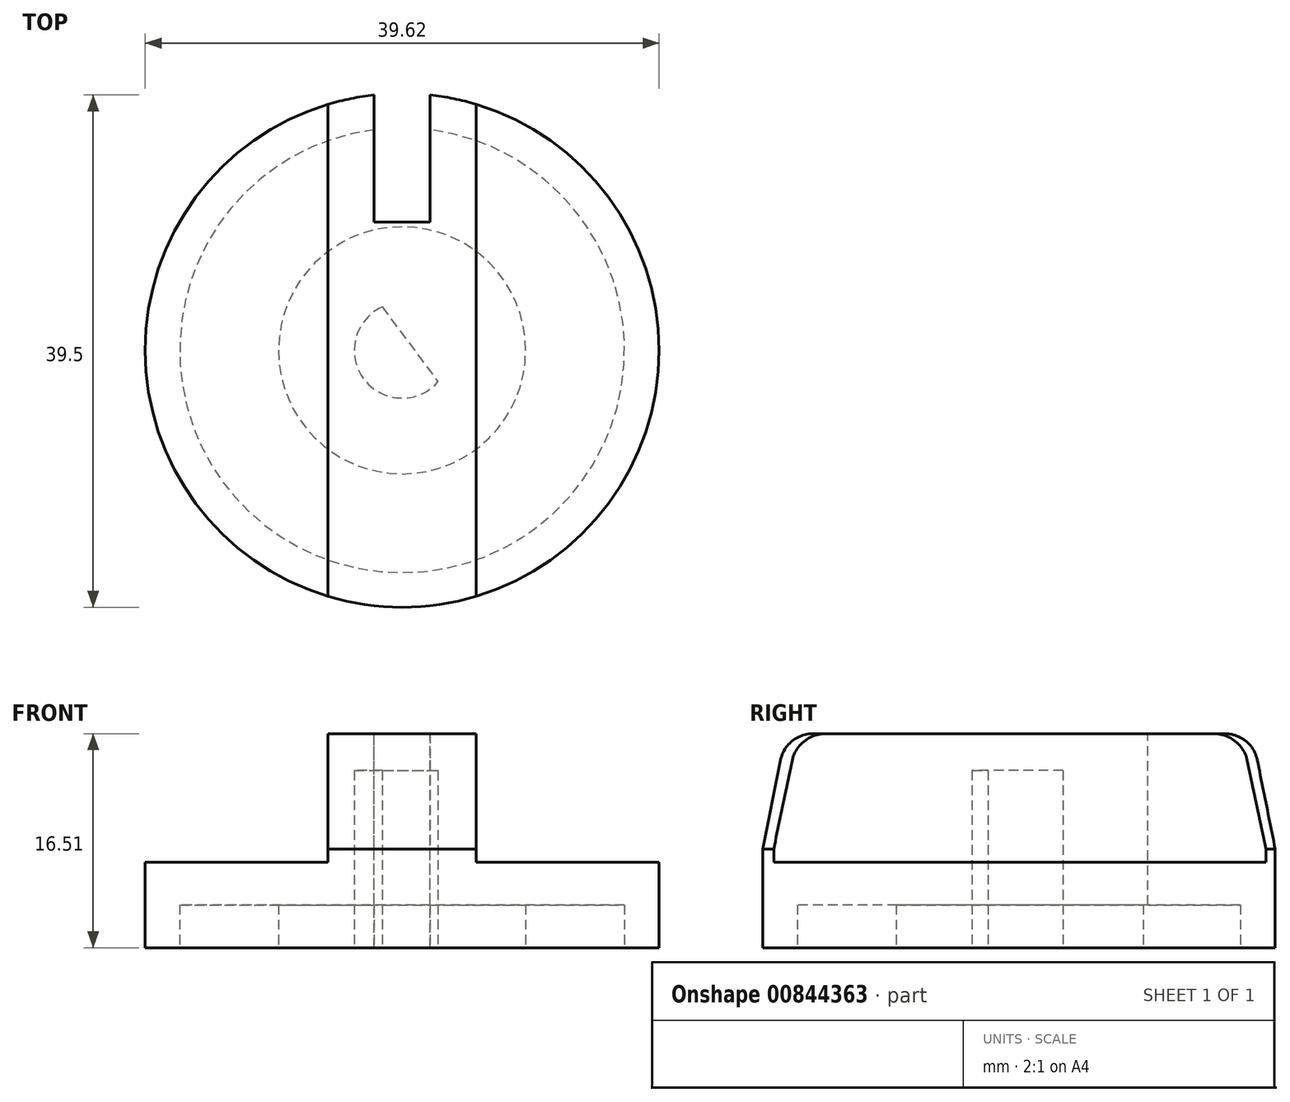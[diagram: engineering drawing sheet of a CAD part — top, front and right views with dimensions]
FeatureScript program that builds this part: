
annotation { "Feature Type Name" : "Feature", "Feature Type Description" : "" }
export const myFeature = defineFeature(function(context is Context, id is Id, definition is map)
    precondition{}
    {
        {
            var Q0;
            Q0=qCreatedBy(makeId("Top.planeOp"),FACE);
            var sketch = newSketch(context, id + "F0", { "sketchPlane" : qUnion([Q0])});
            skCircle(sketch, "E0", {"center": v(0, 0) * mm, "radius": 19.81 * mm});
            skCircle(sketch, "E1", {"center": v(0, 0) * mm, "radius": 3.68 * mm});
            skLineSegment(sketch, "E2", {"start": v(-1.54, 3.34) * mm, "end": v(2.76, -2.43) * mm});
            skSolve(sketch);
        }
        {
            var Q0;
            Q0=makeQuery(id+"F0.imprint","IMPRINT",FACE,{"disambiguationData":[TD([[makeQuery(id+"F0.imprint","IMPRINT",EDGE,{"derivedFrom":sQuery(id+"F0.wireOp",EDGE,"E0")}),1.0]])]});
            var Q1;
            {var subQ0=sQuery(id+"F0.wireOp",EDGE,"E2");Q1=makeQuery(id+"F0.imprint","IMPRINT",FACE,{"disambiguationData":[TD([[makeQuery(id+"F0.imprint","IMPRINT",EDGE,{"derivedFrom":subQ0}),1.0]])]});}
            extrude(context, id + "F1", {"entities" : qUnion([Q0, Q1]), "depth" : 6.6 * mm, "offsetDistance" : 25.4 * mm});
        }
        {
            var Q0;
            Q0=makeQuery(id+"F1.opExtrude","CAP_FACE",FACE,{"disambiguationData":[OSD([sQuery(id+"F0.wireOp",EDGE,"E0"),sQuery(id+"F0.wireOp",EDGE,"E1"),sQuery(id+"F0.wireOp",EDGE,"E2")])],"isStart":true});
            var sketch = newSketch(context, id + "F2", { "sketchPlane" : qUnion([Q0])});
            skCircle(sketch, "E3", {"center": v(0, 0) * mm, "radius": 9.53 * mm});
            skCircle(sketch, "E4", {"center": v(0, 0) * mm, "radius": 17.15 * mm});
            skSolve(sketch);
        }
        {
            var Q0;
            Q0=makeQuery(id+"F2.imprint","IMPRINT",FACE,{"disambiguationData":[TD([[makeQuery(id+"F2.imprint","IMPRINT",EDGE,{"derivedFrom":sQuery(id+"F2.wireOp",EDGE,"E3")}),-1.0]])]});
            extrude(context, id + "F3", {"entities" : qUnion([Q0]), "operationType" : NewBodyOperationType.REMOVE, "oppositeDirection" : true, "depth" : 3.3 * mm, "offsetDistance" : 25.4 * mm});
        }
        {
            var Q0;
            Q0=makeQuery(id+"F1.opExtrude","CAP_FACE",FACE,{"disambiguationData":[OSD([sQuery(id+"F0.wireOp",EDGE,"E0"),sQuery(id+"F0.wireOp",EDGE,"E1"),sQuery(id+"F0.wireOp",EDGE,"E2")])],"isStart":false});
            var sketch = newSketch(context, id + "F4", { "sketchPlane" : qUnion([Q0])});
            skLineSegment(sketch, "E5.bottom", {"start": v(5.72, 18.97) * mm, "end": v(-5.72, 18.97) * mm});
            skLineSegment(sketch, "E5.top", {"start": v(5.72, -18.97) * mm, "end": v(-5.72, -18.97) * mm});
            skLineSegment(sketch, "E5.left", {"start": v(5.72, 18.97) * mm, "end": v(5.72, -18.97) * mm});
            skLineSegment(sketch, "E5.right", {"start": v(-5.72, 18.97) * mm, "end": v(-5.72, -18.97) * mm});
            skPoint(sketch, "E5.middle", {"position": v(0, 0) * mm});
            skSolve(sketch);
        }
        {
            var Q0;
            {var subQ0=sQuery(id+"F4.wireOp",EDGE,"E5.bottom");Q0=makeQuery(id+"F4.imprint","IMPRINT",FACE,{"disambiguationData":[TD([[makeQuery(id+"F4.imprint","IMPRINT",EDGE,{"derivedFrom":subQ0}),-1.0]])]});}
            var Q1;
            Q1=makeQuery(id+"F4.imprint","IMPRINT",FACE,{"disambiguationData":[TD([[makeQuery(id+"F4.imprint","IMPRINT",EDGE,{"derivedFrom":sQuery(id+"F4.wireOp",EDGE,"E5.bottom")}),1.0]])]});
            var Q2;
            {var subQ0=sQuery(id+"F4.wireOp",EDGE,"E5.top");Q2=makeQuery(id+"F4.imprint","IMPRINT",FACE,{"disambiguationData":[TD([[makeQuery(id+"F4.imprint","IMPRINT",EDGE,{"derivedFrom":subQ0}),1.0]])]});}
            extrude(context, id + "F5", {"entities" : qUnion([Q0, Q1, Q2]), "operationType" : NewBodyOperationType.ADD, "depth" : 9.9 * mm, "offsetDistance" : 25.4 * mm});
        }
        {
            var Q0;
            Q0=makeQuery(id+"F5.opExtrude","CAP_FACE",FACE,{"disambiguationData":[OSD([sQuery(id+"F0.wireOp",EDGE,"E0"),sQuery(id+"F0.wireOp",EDGE,"E1"),sQuery(id+"F0.wireOp",EDGE,"E2"),sQuery(id+"F4.wireOp",EDGE,"E5.left"),sQuery(id+"F4.wireOp",EDGE,"E5.right")])],"isStart":false});
            var sketch = newSketch(context, id + "F6", { "sketchPlane" : qUnion([Q0])});
            skLineSegment(sketch, "E6.bottom", {"start": v(-2.15, 19.7) * mm, "end": v(2.15, 19.7) * mm});
            skLineSegment(sketch, "E6.top", {"start": v(-2.15, 9.89) * mm, "end": v(2.15, 9.89) * mm});
            skLineSegment(sketch, "E6.left", {"start": v(-2.15, 19.7) * mm, "end": v(-2.15, 9.89) * mm});
            skLineSegment(sketch, "E6.right", {"start": v(2.15, 19.7) * mm, "end": v(2.15, 9.89) * mm});
            skPoint(sketch, "E6.middle", {"position": v(0, 14.8) * mm});
            skSolve(sketch);
        }
        {
            var Q0;
            Q0=makeQuery(id+"F6.imprint","IMPRINT",FACE,{"disambiguationData":[TD([[makeQuery(id+"F6.imprint","IMPRINT",EDGE,{"derivedFrom":sQuery(id+"F6.wireOp",EDGE,"IdYHg10v-E8hp-SLm5-KDhM-lwTp4nNLskm8")}),1.0]])]});
            var Q1;
            Q1=makeQuery(id+"F6.imprint","IMPRINT",FACE,{"disambiguationData":[TD([[makeQuery(id+"F6.imprint","IMPRINT",EDGE,{"derivedFrom":sQuery(id+"F6.wireOp",EDGE,"E6.bottom")}),-1.0]])]});
            var Q2;
            {var subQ0=sQuery(id+"F6.wireOp",EDGE,"E6.bottom");Q2=makeQuery(id+"F6.imprint","IMPRINT",FACE,{"disambiguationData":[TD([[makeQuery(id+"F6.imprint","IMPRINT",EDGE,{"derivedFrom":subQ0}),1.0]])]});}
            extrude(context, id + "F7", {"entities" : qUnion([Q0, Q1, Q2]), "operationType" : NewBodyOperationType.REMOVE, "oppositeDirection" : true, "depth" : 19.15 * mm, "offsetDistance" : 25.4 * mm});
        }
        {
            var Q0;
            {var subQ0=sQuery(id+"F4.wireOp",EDGE,"E5.bottom");var subQ1=sQuery(id+"F0.wireOp",EDGE,"E0");var subQ2=makeQuery(id+"F1.opExtrude","CAP_EDGE",EDGE,{"disambiguationData":[OSD([subQ1])],"isStart":false});Q0=makeQuery(id+"F5.opExtrude","CAP_EDGE",EDGE,{"disambiguationData":[OSD([subQ1]),TDD([makeQuery(id+"F4.imprint","IMPRINT",EDGE,{"disambiguationData":[TD([[makeQuery(id+"F4.imprint","INTERSECT",VERTEX,{"derivedFrom":[subQ2,subQ0,sQuery(id+"F4.wireOp",EDGE,"E5.left")]}),-1.0]])],"derivedFrom":subQ2})])],"isStart":false});}
            var Q1;
            {var subQ0=sQuery(id+"F4.wireOp",EDGE,"E5.top");var subQ1=sQuery(id+"F0.wireOp",EDGE,"E0");var subQ2=makeQuery(id+"F1.opExtrude","CAP_EDGE",EDGE,{"disambiguationData":[OSD([subQ1])],"isStart":false});Q1=makeQuery(id+"F5.opExtrude","CAP_EDGE",EDGE,{"disambiguationData":[OSD([subQ1]),TDD([makeQuery(id+"F4.imprint","IMPRINT",EDGE,{"disambiguationData":[TD([[makeQuery(id+"F4.imprint","INTERSECT",VERTEX,{"derivedFrom":[subQ2,subQ0,sQuery(id+"F4.wireOp",EDGE,"E5.left")]}),1.0]])],"derivedFrom":subQ2})])],"isStart":false});}
            chamfer(context, id + "F8", {"entities" : qUnion([Q0, Q1]), "chamferType" : ChamferType.TWO_OFFSETS, "width1" : 1.78 * mm, "oppositeDirection" : false, "width2" : 8.9 * mm, "tangentPropagation" : true});
        }
        {
            var Q0;
            {var subQ0=sQuery(id+"F4.wireOp",EDGE,"E5.right");var subQ1=sQuery(id+"F4.wireOp",EDGE,"E5.left");var subQ2=sQuery(id+"F0.wireOp",EDGE,"E0");var subQ3=sQuery(id+"F4.wireOp",EDGE,"E5.bottom");var subQ4=makeQuery(id+"F1.opExtrude","CAP_EDGE",EDGE,{"disambiguationData":[OSD([subQ2])],"isStart":false});Q0=makeQuery(id+"F8.opChamfer","BLEND_EDGE",EDGE,{"blendedFrom":[makeQuery(id+"F5.opExtrude","CAP_EDGE",EDGE,{"disambiguationData":[OSD([subQ2]),TDD([makeQuery(id+"F4.imprint","IMPRINT",EDGE,{"disambiguationData":[TD([[makeQuery(id+"F4.imprint","INTERSECT",VERTEX,{"derivedFrom":[subQ4,subQ3,subQ1]}),-1.0]])],"derivedFrom":subQ4})])],"isStart":false}),makeQuery(id+"F5.opExtrude","CAP_FACE",FACE,{"disambiguationData":[OSD([subQ2,sQuery(id+"F0.wireOp",EDGE,"E1"),sQuery(id+"F0.wireOp",EDGE,"E2"),subQ1,subQ0])],"isStart":false})],"blendedInto":[makeQuery(id+"F5.opExtrude","CAP_FACE",FACE,{"disambiguationData":[OSD([subQ2,sQuery(id+"F0.wireOp",EDGE,"E1"),sQuery(id+"F0.wireOp",EDGE,"E2"),subQ1,subQ0])],"isStart":false})]});}
            var Q1;
            {var subQ0=sQuery(id+"F4.wireOp",EDGE,"E5.right");var subQ1=sQuery(id+"F4.wireOp",EDGE,"E5.left");var subQ2=sQuery(id+"F0.wireOp",EDGE,"E0");var subQ3=sQuery(id+"F4.wireOp",EDGE,"E5.top");var subQ4=makeQuery(id+"F1.opExtrude","CAP_EDGE",EDGE,{"disambiguationData":[OSD([subQ2])],"isStart":false});Q1=makeQuery(id+"F8.opChamfer","BLEND_EDGE",EDGE,{"blendedFrom":[makeQuery(id+"F5.opExtrude","CAP_EDGE",EDGE,{"disambiguationData":[OSD([subQ2]),TDD([makeQuery(id+"F4.imprint","IMPRINT",EDGE,{"disambiguationData":[TD([[makeQuery(id+"F4.imprint","INTERSECT",VERTEX,{"derivedFrom":[subQ4,subQ3,subQ1]}),1.0]])],"derivedFrom":subQ4})])],"isStart":false}),makeQuery(id+"F5.opExtrude","CAP_FACE",FACE,{"disambiguationData":[OSD([subQ2,sQuery(id+"F0.wireOp",EDGE,"E1"),sQuery(id+"F0.wireOp",EDGE,"E2"),subQ1,subQ0])],"isStart":false})],"blendedInto":[makeQuery(id+"F5.opExtrude","CAP_FACE",FACE,{"disambiguationData":[OSD([subQ2,sQuery(id+"F0.wireOp",EDGE,"E1"),sQuery(id+"F0.wireOp",EDGE,"E2"),subQ1,subQ0])],"isStart":false})]});}
            fillet(context, id + "F9", {"entities" : qUnion([Q0, Q1]), "radius" : 2.54 * mm, "tangentPropagation" : true, "allowEdgeOverflow" : false});
        }
        {
            var Q0;
            Q0=makeQuery(id+"F5.opExtrude","CAP_FACE",FACE,{"disambiguationData":[OSD([sQuery(id+"F0.wireOp",EDGE,"E0"),sQuery(id+"F0.wireOp",EDGE,"E1"),sQuery(id+"F0.wireOp",EDGE,"E2"),sQuery(id+"F4.wireOp",EDGE,"E5.left"),sQuery(id+"F4.wireOp",EDGE,"E5.right")])],"isStart":false});
            var sketch = newSketch(context, id + "F10", { "sketchPlane" : qUnion([Q0])});
            skSolve(sketch);
        }
        {
            var Q0;
            Q0=makeQuery(id+"F10.imprint","IMPRINT",FACE,{"disambiguationData":[TD([[makeQuery(id+"F10.imprint","IMPRINT",EDGE,{"derivedFrom":makeQuery(id+"F5.opExtrude","CAP_EDGE",EDGE,{"disambiguationData":[OSD([sQuery(id+"F0.wireOp",EDGE,"E1")])],"isStart":false})}),1.0]])]});
            extrude(context, id + "F11", {"entities" : qUnion([Q0]), "operationType" : NewBodyOperationType.ADD, "oppositeDirection" : true, "depth" : 2.84 * mm, "offsetDistance" : 25.4 * mm});
        }
    });
